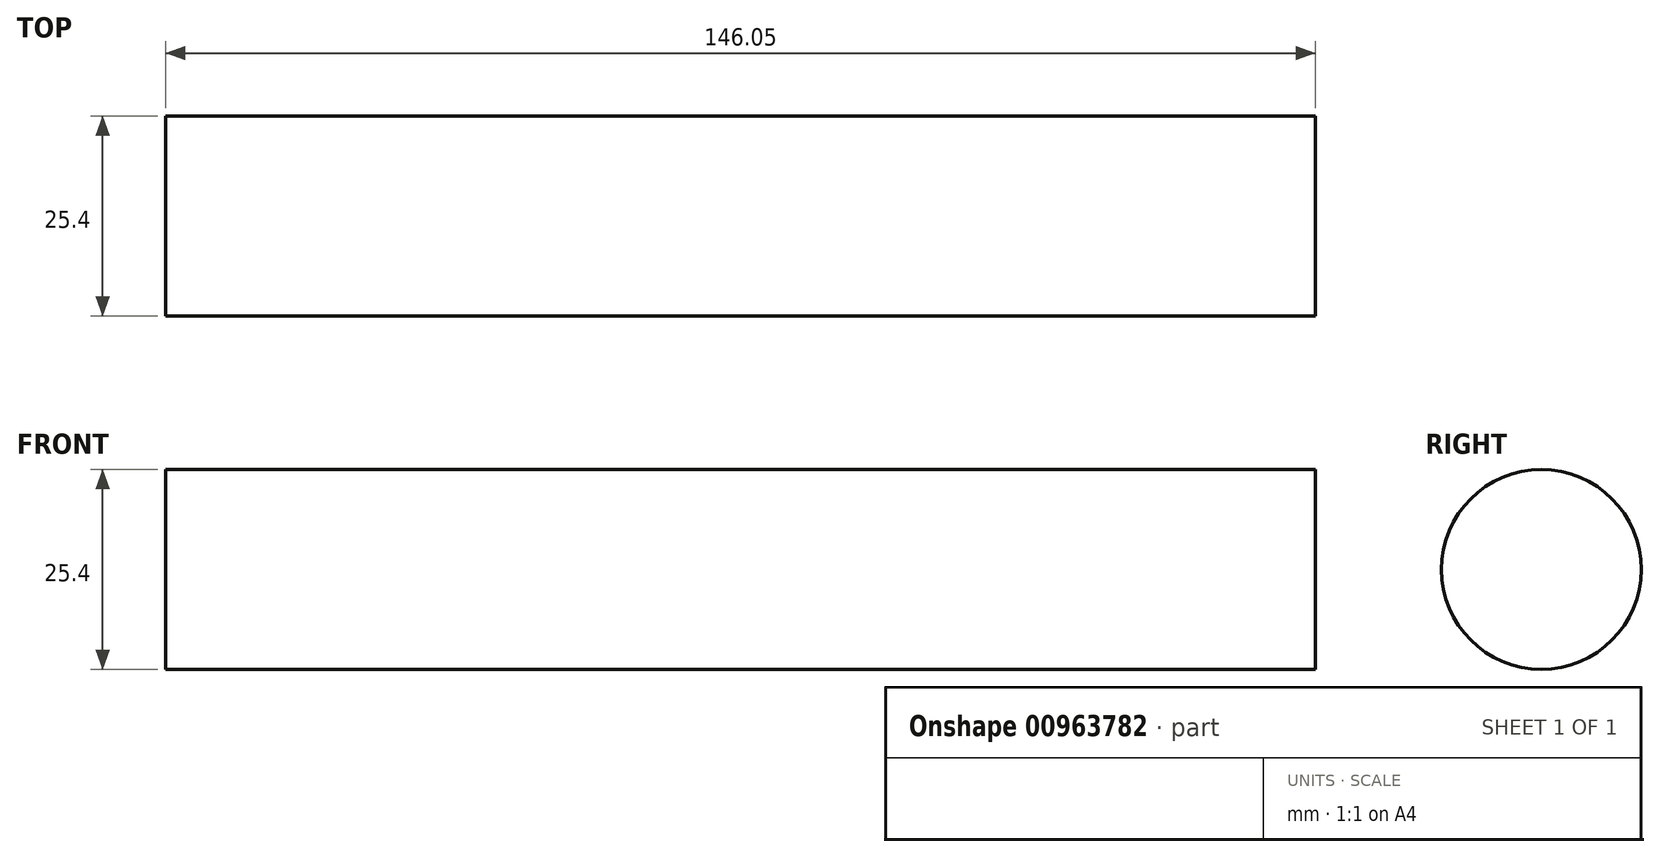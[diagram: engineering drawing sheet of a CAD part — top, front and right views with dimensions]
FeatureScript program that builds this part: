
annotation { "Feature Type Name" : "Feature", "Feature Type Description" : "" }
export const myFeature = defineFeature(function(context is Context, id is Id, definition is map)
    precondition{}
    {
        {
            var Q0;
            Q0=qCreatedBy(makeId("Right.planeOp"),FACE);
            var sketch = newSketch(context, id + "F0", { "sketchPlane" : qUnion([Q0])});
            skCircle(sketch, "E0", {"center": v(0, 0) * mm, "radius": 12.7 * mm});
            skSolve(sketch);
        }
        {
            var Q0;
            Q0 = qSketchRegion(id + "F0", true);
            extrude(context, id + "F1", {"entities" : qUnion([Q0]), "depth" : 146.05 * mm, "offsetDistance" : 25.4 * mm});
        }
    });
